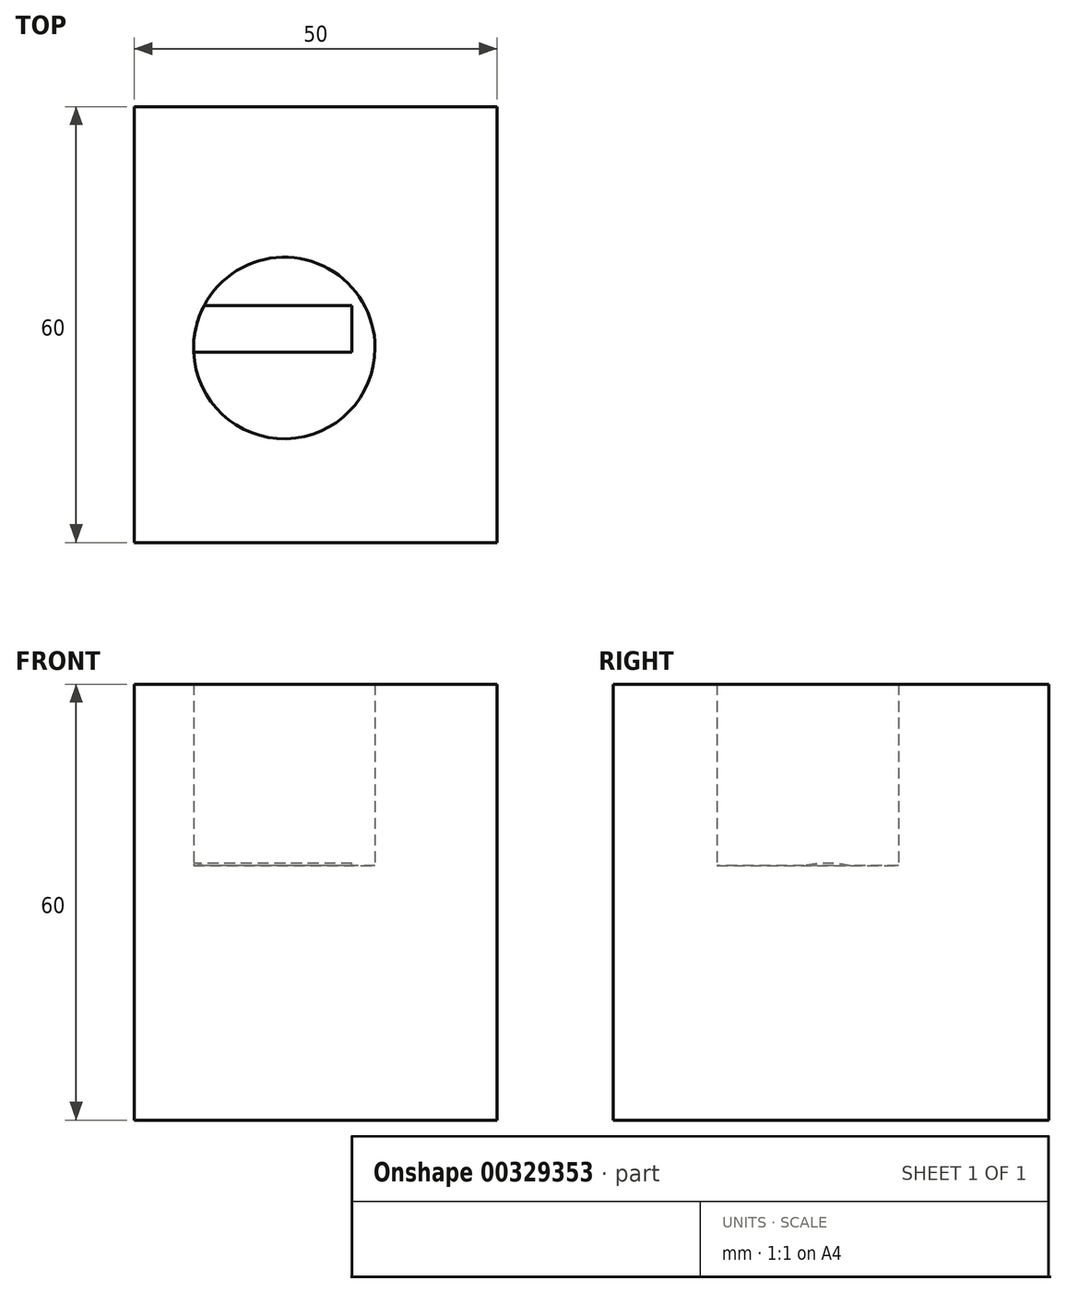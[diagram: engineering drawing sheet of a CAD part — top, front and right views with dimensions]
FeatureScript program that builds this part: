
annotation { "Feature Type Name" : "Feature", "Feature Type Description" : "" }
export const myFeature = defineFeature(function(context is Context, id is Id, definition is map)
    precondition{}
    {
        {
            var Q0;
            Q0=qCreatedBy(makeId("Top.planeOp"),FACE);
            var sketch = newSketch(context, id + "F0", { "sketchPlane" : qUnion([Q0])});
            skLineSegment(sketch, "E0.bottom", {"start": v(0, 0) * mm, "end": v(50, 0) * mm});
            skLineSegment(sketch, "E0.top", {"start": v(0, 60) * mm, "end": v(50, 60) * mm});
            skLineSegment(sketch, "E0.left", {"start": v(0, 0) * mm, "end": v(0, 60) * mm});
            skLineSegment(sketch, "E0.right", {"start": v(50, 0) * mm, "end": v(50, 60) * mm});
            skSolve(sketch);
        }
        {
            var Q0;
            Q0=makeQuery(id+"F0.imprint","IMPRINT",FACE,{"disambiguationData":[TD([[makeQuery(id+"F0.imprint","IMPRINT",EDGE,{"derivedFrom":sQuery(id+"F0.wireOp",EDGE,"E0.bottom")}),1.0]])]});
            extrude(context, id + "F1", {"entities" : qUnion([Q0]), "depth" : 35 * mm});
        }
        {
            var Q0;
            Q0=makeQuery(id+"F1.opExtrude","CAP_FACE",FACE,{"disambiguationData":[OSD([sQuery(id+"F0.wireOp",EDGE,"E0.bottom"),sQuery(id+"F0.wireOp",EDGE,"E0.top"),sQuery(id+"F0.wireOp",EDGE,"E0.left"),sQuery(id+"F0.wireOp",EDGE,"E0.right")])],"isStart":false});
            var sketch = newSketch(context, id + "F2", { "sketchPlane" : qUnion([Q0])});
            skCircle(sketch, "E1", {"center": v(20.67, 26.79) * mm, "radius": 12.5 * mm});
            skSolve(sketch);
        }
        {
            var Q0;
            Q0=makeQuery(id+"F2.imprint","IMPRINT",FACE,{"disambiguationData":[TD([[makeQuery(id+"F2.imprint","IMPRINT",EDGE,{"derivedFrom":sQuery(id+"F2.wireOp",EDGE,"E1")}),-1.0]])]});
            extrude(context, id + "F3", {"entities" : qUnion([Q0]), "operationType" : NewBodyOperationType.ADD, "depth" : 25 * mm});
        }
        {
            var Q0;
            {var subQ0=sQuery(id+"F0.wireOp",EDGE,"E0.left");Q0=makeQuery(id+"F3.boolean.opBoolean","MERGE",FACE,{"derivedFrom":[makeQuery(id+"F1.opExtrude","SWEPT_FACE",FACE,{"disambiguationData":[OSD([subQ0])]}),makeQuery(id+"F3.opExtrude","SWEPT_FACE",FACE,{"disambiguationData":[OSD([subQ0])]})]});}
            var sketch = newSketch(context, id + "F4", { "sketchPlane" : qUnion([Q0])});
            skCircle(sketch, "E2", {"center": v(-29.43, 20.34) * mm, "radius": 15 * mm});
            skSolve(sketch);
        }
        {
            var Q0;
            Q0 = qSketchRegion(id + "F4", true);
            extrude(context, id + "F5", {"entities" : qUnion([Q0]), "operationType" : NewBodyOperationType.ADD, "depth" : -30 * mm});
        }
    });
